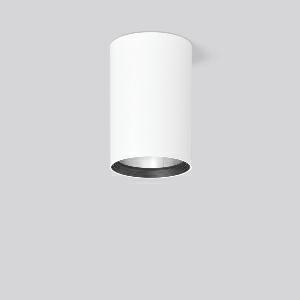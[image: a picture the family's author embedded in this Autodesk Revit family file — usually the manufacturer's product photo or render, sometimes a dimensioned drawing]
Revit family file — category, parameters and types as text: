
# Revit family: heledon_maxi_a_931225_002_76_1808
name_source: partatom
category: Lighting Fixtures
units: mm (PartAtom-declared; Revit-internal decimal feet)

## family parameters
Cut with Voids When Loaded = No
Host = Face
Light Source = No
Part Type = Normal
Room Calculation Point = No
Round Connector Dimension = Use Diameter
Shared = No

## types (1)
- HELEDON maxi A (1 x LED Modul 930, 4350 lm, 3000)
    Apparent Load = 35 VA
    Approval mark = CE
    CIE Flux Codes = 100 100 100 100 100
    Color Rendering = 90
    Color Temperature = 3000
    Default Elevation = 1800 mm
    Description = Series: HELEDON maxi
Cylindrical surface-mounted downlight. Housing: die-cast aluminium, powder-coated. Internal ceiling frame polycarbonate with bayonet mounting. Black plastic ring and recessed LED to prevent glare from the side. Optical assembly with reflector made of MIRO-Silver with 98% total light reflection for outstanding efficiency - can be changed without tools. Best colour rendering index Ra>90. Suitable for Ceiling mounting. Easy installation with a separate ceiling frame with bayonet mounting and plug connection. Driver integrated. Connected via plug-in connector. High quality converter without flickering and stroboscopic effect. The following accessories can be mounted without use of tools: interchangeable lenses, decorative glasses, honeycomb louvre, clear and frosted diffusers, white interchangeable plastic ring. 
Colour: traffic white, matt (RAL 9016)
Diameter: 123 mm
Height: 183 mm
Lamp: LED
Socket: without socket
Colour temperature: 3000K
Colour rendering index (CRI): 92
System power: 35 W
Rated luminous flux: 4350 lm
Luminous efficiency: 124 lm/W
Control gear: Converter, dimmable, DALI
Protection class: I
Type of protection: IP 20
    Height = 183 mm
    Lamp = 1 x LED Modul 930
    Lamp Light Flux = 4350 lm
    Lamp count = 1
    Length = 123 mm
    Lifetime = 50000 h
    Luminous efficacy = 124 lm/W
    Manufacturer = RZB
    ModVariant = No
    Model = 931225.002.76
    Mounting Place = Ceiling
    Mounting Type = Surface mounted
    Number of Poles = 1
    OnlyDefault = Yes
    Power Factor = 1
    Product Name = HELEDON maxi A
    Product group = Surface mounted downlights
    ProductGroupID = 302
    Protection Class = Protection class I
    Protection Degree = IP 20
    RLX_Detail_Level = 1
    RLX_Emergency_Light_Flux = 0 lm
    RLX_Emergency_Type = 0
    RLX_Emergency_Type_DB = No
    RlxData = <blob elided: 97553 chars, md5=5020cebc>
    Socket = socket
    Standby Power = 0 W
    System Light Flux = 4350 lm
    System Power = 35 W
    Type Comments = Product without accessories
    Type Image = 931192.002.jpg
    URL = http://relux.com
    VarID = ---
    Voltage = 230 V
    Voltage Range = 220-240 V
    Weight = 0.00 kg
    Width = 0 mm  [stored 0 ft]

note: [stored X ft] marks values corroborated as IEEE doubles in the binary element streams (Revit-internal decimal feet)

## geometry (parser evidence)
native form markers: Blend x4, Sweep x9
no freeform markers — native parametric forms only
